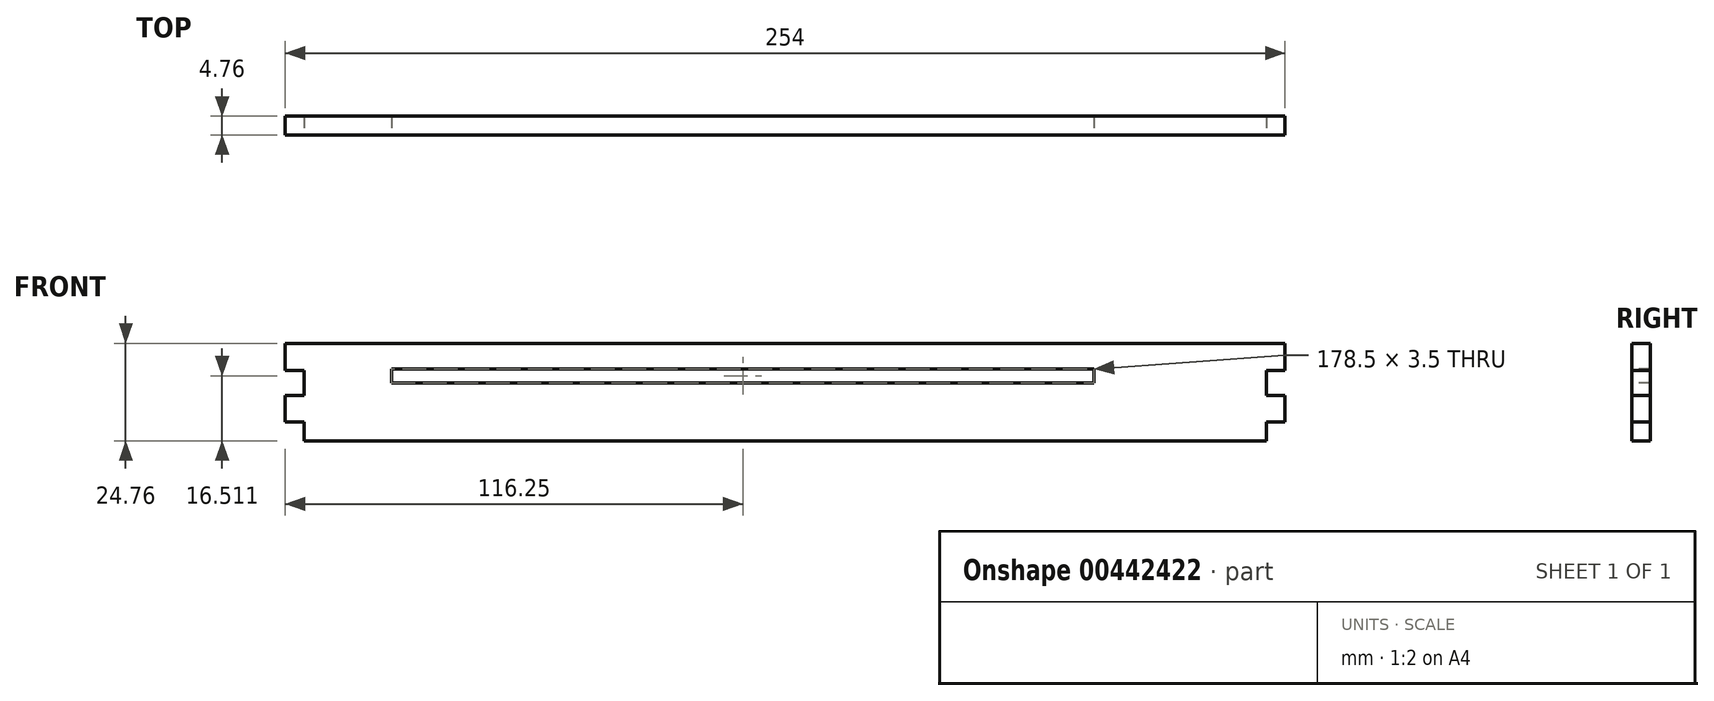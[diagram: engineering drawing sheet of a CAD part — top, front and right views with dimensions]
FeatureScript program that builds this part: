
annotation { "Feature Type Name" : "Feature", "Feature Type Description" : "" }
export const myFeature = defineFeature(function(context is Context, id is Id, definition is map)
    precondition{}
    {
        {
            var Q0;
            Q0=qCreatedBy(makeId("Front.planeOp"),FACE);
            var sketch = newSketch(context, id + "F0", { "sketchPlane" : qUnion([Q0])});
            skLineSegment(sketch, "E0.bottom", {"start": v(-127, 12.38) * mm, "end": v(127, 12.38) * mm});
            skLineSegment(sketch, "E0.top", {"start": v(-127, -12.38) * mm, "end": v(127, -12.38) * mm});
            skLineSegment(sketch, "E0.left", {"start": v(-127, 12.38) * mm, "end": v(-127, -12.38) * mm});
            skLineSegment(sketch, "E0.right", {"start": v(127, 12.38) * mm, "end": v(127, -12.38) * mm});
            skPoint(sketch, "E0.middle", {"position": v(0, 0) * mm});
            skSolve(sketch);
        }
        {
            var Q0;
            Q0 = qSketchRegion(id + "F0", true);
            extrude(context, id + "F1", {"entities" : qUnion([Q0]), "depth" : 4.76 * mm});
        }
        {
            var Q0;
            Q0=makeQuery(id+"F1.opExtrude","CAP_FACE",FACE,{"disambiguationData":[OSD([sQuery(id+"F0.wireOp",EDGE,"E0.bottom"),sQuery(id+"F0.wireOp",EDGE,"E0.top"),sQuery(id+"F0.wireOp",EDGE,"E0.left"),sQuery(id+"F0.wireOp",EDGE,"E0.right")])],"isStart":false});
            var sketch = newSketch(context, id + "F2", { "sketchPlane" : qUnion([Q0])});
            skLineSegment(sketch, "E1", {"start": v(-127, -7.62) * mm, "end": v(-127, 12.38) * mm, "construction": true});
            skLineSegment(sketch, "E2", {"start": v(-127, 2.38) * mm, "end": v(127, 2.38) * mm, "construction": true});
            skLineSegment(sketch, "E3.bottom", {"start": v(-122.24, 5.56) * mm, "end": v(-127, 5.56) * mm});
            skLineSegment(sketch, "E3.top", {"start": v(-122.24, -0.8) * mm, "end": v(-127, -0.8) * mm});
            skLineSegment(sketch, "E3.left", {"start": v(-122.24, 5.56) * mm, "end": v(-122.24, -0.8) * mm});
            skLineSegment(sketch, "E3.right", {"start": v(-127, 5.56) * mm, "end": v(-127, -0.8) * mm});
            skLineSegment(sketch, "E4", {"start": v(0, 0) * mm, "end": v(0, 12.38) * mm, "construction": true});
            skLineSegment(sketch, "E5.MirrorCS", {"start": v(122.24, 5.56) * mm, "end": v(127, 5.56) * mm});
            skLineSegment(sketch, "E6.MirrorCS", {"start": v(122.24, 5.56) * mm, "end": v(122.24, -0.8) * mm});
            skLineSegment(sketch, "E7.MirrorCS", {"start": v(122.24, -0.8) * mm, "end": v(127, -0.8) * mm});
            skLineSegment(sketch, "E8", {"start": v(127, 5.56) * mm, "end": v(127, -0.8) * mm});
            skLineSegment(sketch, "E9", {"start": v(127, -12.38) * mm, "end": v(-127, -12.38) * mm, "construction": true});
            skLineSegment(sketch, "E10", {"start": v(-127, -7.62) * mm, "end": v(127, -7.62) * mm, "construction": true});
            skSolve(sketch);
        }
        {
            var Q0;
            Q0 = qSketchRegion(id + "F2", true);
            extrude(context, id + "F3", {"entities" : qUnion([Q0]), "operationType" : NewBodyOperationType.REMOVE, "oppositeDirection" : true, "depth" : 25.4 * mm});
        }
        {
            var Q0;
            Q0=makeQuery(id+"F1.opExtrude","CAP_FACE",FACE,{"disambiguationData":[OSD([sQuery(id+"F0.wireOp",EDGE,"E0.bottom"),sQuery(id+"F0.wireOp",EDGE,"E0.top"),sQuery(id+"F0.wireOp",EDGE,"E0.left"),sQuery(id+"F0.wireOp",EDGE,"E0.right")])],"isStart":false});
            var sketch = newSketch(context, id + "F4", { "sketchPlane" : qUnion([Q0])});
            skLineSegment(sketch, "E11", {"start": v(127, -12.38) * mm, "end": v(122.24, -12.38) * mm});
            skLineSegment(sketch, "E12", {"start": v(122.24, -12.38) * mm, "end": v(122.24, -7.62) * mm});
            skLineSegment(sketch, "E13", {"start": v(122.24, -7.62) * mm, "end": v(127, -7.62) * mm});
            skLineSegment(sketch, "E14", {"start": v(127, -7.62) * mm, "end": v(127, -12.38) * mm});
            skLineSegment(sketch, "E15", {"start": v(0, 0) * mm, "end": v(0, 12.38) * mm, "construction": true});
            skLineSegment(sketch, "E16.MirrorCS", {"start": v(-122.24, -12.38) * mm, "end": v(-122.24, -7.62) * mm});
            skLineSegment(sketch, "E17.MirrorCS", {"start": v(-122.24, -7.62) * mm, "end": v(-127, -7.62) * mm});
            skLineSegment(sketch, "E18.MirrorCS", {"start": v(-127, -7.62) * mm, "end": v(-127, -12.38) * mm});
            skLineSegment(sketch, "E19.MirrorCS", {"start": v(-127, -12.38) * mm, "end": v(-122.24, -12.38) * mm});
            skSolve(sketch);
        }
        {
            var Q0;
            Q0 = qSketchRegion(id + "F4", true);
            extrude(context, id + "F5", {"entities" : qUnion([Q0]), "operationType" : NewBodyOperationType.REMOVE, "oppositeDirection" : true, "depth" : 25.4 * mm});
        }
        {
            var Q0;
            Q0=makeQuery(id+"F1.opExtrude","CAP_FACE",FACE,{"disambiguationData":[OSD([sQuery(id+"F0.wireOp",EDGE,"E0.bottom"),sQuery(id+"F0.wireOp",EDGE,"E0.top"),sQuery(id+"F0.wireOp",EDGE,"E0.left"),sQuery(id+"F0.wireOp",EDGE,"E0.right")])],"isStart":false});
            var sketch = newSketch(context, id + "F6", { "sketchPlane" : qUnion([Q0])});
            skLineSegment(sketch, "E20", {"start": v(-110, 12.38) * mm, "end": v(-110, -12.38) * mm, "construction": true});
            skLineSegment(sketch, "E21.bottom", {"start": v(-100, 2.38) * mm, "end": v(-92, 2.38) * mm});
            skLineSegment(sketch, "E21.top", {"start": v(-100, 5.88) * mm, "end": v(-92, 5.88) * mm});
            skLineSegment(sketch, "E21.left", {"start": v(-100, 2.38) * mm, "end": v(-100, 5.88) * mm});
            skLineSegment(sketch, "E21.right", {"start": v(-92, 2.38) * mm, "end": v(-92, 5.88) * mm});
            skLineSegment(sketch, "E22", {"start": v(-96, 5.88) * mm, "end": v(-96, 2.38) * mm, "construction": true});
            skLineSegment(sketch, "E23", {"start": v(-100, 2.38) * mm, "end": v(-122.24, 2.38) * mm, "construction": true});
            skLineSegment(sketch, "E24.1.0.0", {"start": v(-90.5, 5.88) * mm, "end": v(-90.5, 2.38) * mm, "construction": true});
            skLineSegment(sketch, "E24.1.0.1", {"start": v(-94.5, 5.88) * mm, "end": v(-86.5, 5.88) * mm});
            skLineSegment(sketch, "E24.1.0.2", {"start": v(-94.5, 2.38) * mm, "end": v(-94.5, 5.88) * mm});
            skLineSegment(sketch, "E24.1.0.3", {"start": v(-94.5, 2.38) * mm, "end": v(-86.5, 2.38) * mm});
            skLineSegment(sketch, "E24.1.0.4", {"start": v(-86.5, 2.38) * mm, "end": v(-86.5, 5.88) * mm});
            skLineSegment(sketch, "E24.2.0.0", {"start": v(-85, 5.88) * mm, "end": v(-85, 2.38) * mm, "construction": true});
            skLineSegment(sketch, "E24.2.0.1", {"start": v(-89, 5.88) * mm, "end": v(-81, 5.88) * mm});
            skLineSegment(sketch, "E24.2.0.2", {"start": v(-89, 2.38) * mm, "end": v(-89, 5.88) * mm});
            skLineSegment(sketch, "E24.2.0.3", {"start": v(-89, 2.38) * mm, "end": v(-81, 2.38) * mm});
            skLineSegment(sketch, "E24.2.0.4", {"start": v(-81, 2.38) * mm, "end": v(-81, 5.88) * mm});
            skLineSegment(sketch, "E24.3.0.0", {"start": v(-79.5, 5.88) * mm, "end": v(-79.5, 2.38) * mm, "construction": true});
            skLineSegment(sketch, "E24.3.0.1", {"start": v(-83.5, 5.88) * mm, "end": v(-75.5, 5.88) * mm});
            skLineSegment(sketch, "E24.3.0.2", {"start": v(-83.5, 2.38) * mm, "end": v(-83.5, 5.88) * mm});
            skLineSegment(sketch, "E24.3.0.3", {"start": v(-83.5, 2.38) * mm, "end": v(-75.5, 2.38) * mm});
            skLineSegment(sketch, "E24.3.0.4", {"start": v(-75.5, 2.38) * mm, "end": v(-75.5, 5.88) * mm});
            skLineSegment(sketch, "E24.4.0.0", {"start": v(-74, 5.88) * mm, "end": v(-74, 2.38) * mm, "construction": true});
            skLineSegment(sketch, "E24.4.0.1", {"start": v(-78, 5.88) * mm, "end": v(-70, 5.88) * mm});
            skLineSegment(sketch, "E24.4.0.2", {"start": v(-78, 2.38) * mm, "end": v(-78, 5.88) * mm});
            skLineSegment(sketch, "E24.4.0.3", {"start": v(-78, 2.38) * mm, "end": v(-70, 2.38) * mm});
            skLineSegment(sketch, "E24.4.0.4", {"start": v(-70, 2.38) * mm, "end": v(-70, 5.88) * mm});
            skLineSegment(sketch, "E24.5.0.0", {"start": v(-68.5, 5.88) * mm, "end": v(-68.5, 2.38) * mm, "construction": true});
            skLineSegment(sketch, "E24.5.0.1", {"start": v(-72.5, 5.88) * mm, "end": v(-64.5, 5.88) * mm});
            skLineSegment(sketch, "E24.5.0.2", {"start": v(-72.5, 2.38) * mm, "end": v(-72.5, 5.88) * mm});
            skLineSegment(sketch, "E24.5.0.3", {"start": v(-72.5, 2.38) * mm, "end": v(-64.5, 2.38) * mm});
            skLineSegment(sketch, "E24.5.0.4", {"start": v(-64.5, 2.38) * mm, "end": v(-64.5, 5.88) * mm});
            skLineSegment(sketch, "E24.6.0.0", {"start": v(-63, 5.88) * mm, "end": v(-63, 2.38) * mm, "construction": true});
            skLineSegment(sketch, "E24.6.0.1", {"start": v(-67, 5.88) * mm, "end": v(-59, 5.88) * mm});
            skLineSegment(sketch, "E24.6.0.2", {"start": v(-67, 2.38) * mm, "end": v(-67, 5.88) * mm});
            skLineSegment(sketch, "E24.6.0.3", {"start": v(-67, 2.38) * mm, "end": v(-59, 2.38) * mm});
            skLineSegment(sketch, "E24.6.0.4", {"start": v(-59, 2.38) * mm, "end": v(-59, 5.88) * mm});
            skLineSegment(sketch, "E24.7.0.0", {"start": v(-57.5, 5.88) * mm, "end": v(-57.5, 2.38) * mm, "construction": true});
            skLineSegment(sketch, "E24.7.0.1", {"start": v(-61.5, 5.88) * mm, "end": v(-53.5, 5.88) * mm});
            skLineSegment(sketch, "E24.7.0.2", {"start": v(-61.5, 2.38) * mm, "end": v(-61.5, 5.88) * mm});
            skLineSegment(sketch, "E24.7.0.3", {"start": v(-61.5, 2.38) * mm, "end": v(-53.5, 2.38) * mm});
            skLineSegment(sketch, "E24.7.0.4", {"start": v(-53.5, 2.38) * mm, "end": v(-53.5, 5.88) * mm});
            skLineSegment(sketch, "E24.8.0.0", {"start": v(-52, 5.88) * mm, "end": v(-52, 2.38) * mm, "construction": true});
            skLineSegment(sketch, "E24.8.0.1", {"start": v(-56, 5.88) * mm, "end": v(-48, 5.88) * mm});
            skLineSegment(sketch, "E24.8.0.2", {"start": v(-56, 2.38) * mm, "end": v(-56, 5.88) * mm});
            skLineSegment(sketch, "E24.8.0.3", {"start": v(-56, 2.38) * mm, "end": v(-48, 2.38) * mm});
            skLineSegment(sketch, "E24.8.0.4", {"start": v(-48, 2.38) * mm, "end": v(-48, 5.88) * mm});
            skLineSegment(sketch, "E24.9.0.0", {"start": v(-46.5, 5.88) * mm, "end": v(-46.5, 2.38) * mm, "construction": true});
            skLineSegment(sketch, "E24.9.0.1", {"start": v(-50.5, 5.88) * mm, "end": v(-42.5, 5.88) * mm});
            skLineSegment(sketch, "E24.9.0.2", {"start": v(-50.5, 2.38) * mm, "end": v(-50.5, 5.88) * mm});
            skLineSegment(sketch, "E24.9.0.3", {"start": v(-50.5, 2.38) * mm, "end": v(-42.5, 2.38) * mm});
            skLineSegment(sketch, "E24.9.0.4", {"start": v(-42.5, 2.38) * mm, "end": v(-42.5, 5.88) * mm});
            skLineSegment(sketch, "E24.10.0.0", {"start": v(-41, 5.88) * mm, "end": v(-41, 2.38) * mm, "construction": true});
            skLineSegment(sketch, "E24.10.0.1", {"start": v(-45, 5.88) * mm, "end": v(-37, 5.88) * mm});
            skLineSegment(sketch, "E24.10.0.2", {"start": v(-45, 2.38) * mm, "end": v(-45, 5.88) * mm});
            skLineSegment(sketch, "E24.10.0.3", {"start": v(-45, 2.38) * mm, "end": v(-37, 2.38) * mm});
            skLineSegment(sketch, "E24.10.0.4", {"start": v(-37, 2.38) * mm, "end": v(-37, 5.88) * mm});
            skLineSegment(sketch, "E24.11.0.0", {"start": v(-35.5, 5.88) * mm, "end": v(-35.5, 2.38) * mm, "construction": true});
            skLineSegment(sketch, "E24.11.0.1", {"start": v(-39.5, 5.88) * mm, "end": v(-31.5, 5.88) * mm});
            skLineSegment(sketch, "E24.11.0.2", {"start": v(-39.5, 2.38) * mm, "end": v(-39.5, 5.88) * mm});
            skLineSegment(sketch, "E24.11.0.3", {"start": v(-39.5, 2.38) * mm, "end": v(-31.5, 2.38) * mm});
            skLineSegment(sketch, "E24.11.0.4", {"start": v(-31.5, 2.38) * mm, "end": v(-31.5, 5.88) * mm});
            skLineSegment(sketch, "E24.12.0.0", {"start": v(-30, 5.88) * mm, "end": v(-30, 2.38) * mm, "construction": true});
            skLineSegment(sketch, "E24.12.0.1", {"start": v(-34, 5.88) * mm, "end": v(-26, 5.88) * mm});
            skLineSegment(sketch, "E24.12.0.2", {"start": v(-34, 2.38) * mm, "end": v(-34, 5.88) * mm});
            skLineSegment(sketch, "E24.12.0.3", {"start": v(-34, 2.38) * mm, "end": v(-26, 2.38) * mm});
            skLineSegment(sketch, "E24.12.0.4", {"start": v(-26, 2.38) * mm, "end": v(-26, 5.88) * mm});
            skLineSegment(sketch, "E24.13.0.0", {"start": v(-24.5, 5.88) * mm, "end": v(-24.5, 2.38) * mm, "construction": true});
            skLineSegment(sketch, "E24.13.0.1", {"start": v(-28.5, 5.88) * mm, "end": v(-20.5, 5.88) * mm});
            skLineSegment(sketch, "E24.13.0.2", {"start": v(-28.5, 2.38) * mm, "end": v(-28.5, 5.88) * mm});
            skLineSegment(sketch, "E24.13.0.3", {"start": v(-28.5, 2.38) * mm, "end": v(-20.5, 2.38) * mm});
            skLineSegment(sketch, "E24.13.0.4", {"start": v(-20.5, 2.38) * mm, "end": v(-20.5, 5.88) * mm});
            skLineSegment(sketch, "E24.14.0.0", {"start": v(-19, 5.88) * mm, "end": v(-19, 2.38) * mm, "construction": true});
            skLineSegment(sketch, "E24.14.0.1", {"start": v(-23, 5.88) * mm, "end": v(-15, 5.88) * mm});
            skLineSegment(sketch, "E24.14.0.2", {"start": v(-23, 2.38) * mm, "end": v(-23, 5.88) * mm});
            skLineSegment(sketch, "E24.14.0.3", {"start": v(-23, 2.38) * mm, "end": v(-15, 2.38) * mm});
            skLineSegment(sketch, "E24.14.0.4", {"start": v(-15, 2.38) * mm, "end": v(-15, 5.88) * mm});
            skLineSegment(sketch, "E24.15.0.0", {"start": v(-13.5, 5.88) * mm, "end": v(-13.5, 2.38) * mm, "construction": true});
            skLineSegment(sketch, "E24.15.0.1", {"start": v(-17.5, 5.88) * mm, "end": v(-9.5, 5.88) * mm});
            skLineSegment(sketch, "E24.15.0.2", {"start": v(-17.5, 2.38) * mm, "end": v(-17.5, 5.88) * mm});
            skLineSegment(sketch, "E24.15.0.3", {"start": v(-17.5, 2.38) * mm, "end": v(-9.5, 2.38) * mm});
            skLineSegment(sketch, "E24.15.0.4", {"start": v(-9.5, 2.38) * mm, "end": v(-9.5, 5.88) * mm});
            skLineSegment(sketch, "E24.16.0.0", {"start": v(-8, 5.88) * mm, "end": v(-8, 2.38) * mm, "construction": true});
            skLineSegment(sketch, "E24.16.0.1", {"start": v(-12, 5.88) * mm, "end": v(-4, 5.88) * mm});
            skLineSegment(sketch, "E24.16.0.2", {"start": v(-12, 2.38) * mm, "end": v(-12, 5.88) * mm});
            skLineSegment(sketch, "E24.16.0.3", {"start": v(-12, 2.38) * mm, "end": v(-4, 2.38) * mm});
            skLineSegment(sketch, "E24.16.0.4", {"start": v(-4, 2.38) * mm, "end": v(-4, 5.88) * mm});
            skLineSegment(sketch, "E24.17.0.0", {"start": v(-2.5, 5.88) * mm, "end": v(-2.5, 2.38) * mm, "construction": true});
            skLineSegment(sketch, "E24.17.0.1", {"start": v(-6.5, 5.88) * mm, "end": v(1.5, 5.88) * mm});
            skLineSegment(sketch, "E24.17.0.2", {"start": v(-6.5, 2.38) * mm, "end": v(-6.5, 5.88) * mm});
            skLineSegment(sketch, "E24.17.0.3", {"start": v(-6.5, 2.38) * mm, "end": v(1.5, 2.38) * mm});
            skLineSegment(sketch, "E24.17.0.4", {"start": v(1.5, 2.38) * mm, "end": v(1.5, 5.88) * mm});
            skLineSegment(sketch, "E24.18.0.0", {"start": v(3, 5.88) * mm, "end": v(3, 2.38) * mm, "construction": true});
            skLineSegment(sketch, "E24.18.0.1", {"start": v(-1, 5.88) * mm, "end": v(7, 5.88) * mm});
            skLineSegment(sketch, "E24.18.0.2", {"start": v(-1, 2.38) * mm, "end": v(-1, 5.88) * mm});
            skLineSegment(sketch, "E24.18.0.3", {"start": v(-1, 2.38) * mm, "end": v(7, 2.38) * mm});
            skLineSegment(sketch, "E24.18.0.4", {"start": v(7, 2.38) * mm, "end": v(7, 5.88) * mm});
            skLineSegment(sketch, "E24.19.0.0", {"start": v(8.5, 5.88) * mm, "end": v(8.5, 2.38) * mm, "construction": true});
            skLineSegment(sketch, "E24.19.0.1", {"start": v(4.5, 5.88) * mm, "end": v(12.5, 5.88) * mm});
            skLineSegment(sketch, "E24.19.0.2", {"start": v(4.5, 2.38) * mm, "end": v(4.5, 5.88) * mm});
            skLineSegment(sketch, "E24.19.0.3", {"start": v(4.5, 2.38) * mm, "end": v(12.5, 2.38) * mm});
            skLineSegment(sketch, "E24.19.0.4", {"start": v(12.5, 2.38) * mm, "end": v(12.5, 5.88) * mm});
            skLineSegment(sketch, "E24.20.0.0", {"start": v(14, 5.88) * mm, "end": v(14, 2.38) * mm, "construction": true});
            skLineSegment(sketch, "E24.20.0.1", {"start": v(10, 5.88) * mm, "end": v(18, 5.88) * mm});
            skLineSegment(sketch, "E24.20.0.2", {"start": v(10, 2.38) * mm, "end": v(10, 5.88) * mm});
            skLineSegment(sketch, "E24.20.0.3", {"start": v(10, 2.38) * mm, "end": v(18, 2.38) * mm});
            skLineSegment(sketch, "E24.20.0.4", {"start": v(18, 2.38) * mm, "end": v(18, 5.88) * mm});
            skLineSegment(sketch, "E24.21.0.0", {"start": v(19.5, 5.88) * mm, "end": v(19.5, 2.38) * mm, "construction": true});
            skLineSegment(sketch, "E24.21.0.1", {"start": v(15.5, 5.88) * mm, "end": v(23.5, 5.88) * mm});
            skLineSegment(sketch, "E24.21.0.2", {"start": v(15.5, 2.38) * mm, "end": v(15.5, 5.88) * mm});
            skLineSegment(sketch, "E24.21.0.3", {"start": v(15.5, 2.38) * mm, "end": v(23.5, 2.38) * mm});
            skLineSegment(sketch, "E24.21.0.4", {"start": v(23.5, 2.38) * mm, "end": v(23.5, 5.88) * mm});
            skLineSegment(sketch, "E24.22.0.0", {"start": v(25, 5.88) * mm, "end": v(25, 2.38) * mm, "construction": true});
            skLineSegment(sketch, "E24.22.0.1", {"start": v(21, 5.88) * mm, "end": v(29, 5.88) * mm});
            skLineSegment(sketch, "E24.22.0.2", {"start": v(21, 2.38) * mm, "end": v(21, 5.88) * mm});
            skLineSegment(sketch, "E24.22.0.3", {"start": v(21, 2.38) * mm, "end": v(29, 2.38) * mm});
            skLineSegment(sketch, "E24.22.0.4", {"start": v(29, 2.38) * mm, "end": v(29, 5.88) * mm});
            skLineSegment(sketch, "E24.23.0.0", {"start": v(30.5, 5.88) * mm, "end": v(30.5, 2.38) * mm, "construction": true});
            skLineSegment(sketch, "E24.23.0.1", {"start": v(26.5, 5.88) * mm, "end": v(34.5, 5.88) * mm});
            skLineSegment(sketch, "E24.23.0.2", {"start": v(26.5, 2.38) * mm, "end": v(26.5, 5.88) * mm});
            skLineSegment(sketch, "E24.23.0.3", {"start": v(26.5, 2.38) * mm, "end": v(34.5, 2.38) * mm});
            skLineSegment(sketch, "E24.23.0.4", {"start": v(34.5, 2.38) * mm, "end": v(34.5, 5.88) * mm});
            skLineSegment(sketch, "E24.24.0.0", {"start": v(36, 5.88) * mm, "end": v(36, 2.38) * mm, "construction": true});
            skLineSegment(sketch, "E24.24.0.1", {"start": v(32, 5.88) * mm, "end": v(40, 5.88) * mm});
            skLineSegment(sketch, "E24.24.0.2", {"start": v(32, 2.38) * mm, "end": v(32, 5.88) * mm});
            skLineSegment(sketch, "E24.24.0.3", {"start": v(32, 2.38) * mm, "end": v(40, 2.38) * mm});
            skLineSegment(sketch, "E24.24.0.4", {"start": v(40, 2.38) * mm, "end": v(40, 5.88) * mm});
            skLineSegment(sketch, "E24.25.0.0", {"start": v(41.5, 5.88) * mm, "end": v(41.5, 2.38) * mm, "construction": true});
            skLineSegment(sketch, "E24.25.0.1", {"start": v(37.5, 5.88) * mm, "end": v(45.5, 5.88) * mm});
            skLineSegment(sketch, "E24.25.0.2", {"start": v(37.5, 2.38) * mm, "end": v(37.5, 5.88) * mm});
            skLineSegment(sketch, "E24.25.0.3", {"start": v(37.5, 2.38) * mm, "end": v(45.5, 2.38) * mm});
            skLineSegment(sketch, "E24.25.0.4", {"start": v(45.5, 2.38) * mm, "end": v(45.5, 5.88) * mm});
            skLineSegment(sketch, "E24.26.0.0", {"start": v(47, 5.88) * mm, "end": v(47, 2.38) * mm, "construction": true});
            skLineSegment(sketch, "E24.26.0.1", {"start": v(43, 5.88) * mm, "end": v(51, 5.88) * mm});
            skLineSegment(sketch, "E24.26.0.2", {"start": v(43, 2.38) * mm, "end": v(43, 5.88) * mm});
            skLineSegment(sketch, "E24.26.0.3", {"start": v(43, 2.38) * mm, "end": v(51, 2.38) * mm});
            skLineSegment(sketch, "E24.26.0.4", {"start": v(51, 2.38) * mm, "end": v(51, 5.88) * mm});
            skLineSegment(sketch, "E24.27.0.0", {"start": v(52.5, 5.88) * mm, "end": v(52.5, 2.38) * mm, "construction": true});
            skLineSegment(sketch, "E24.27.0.1", {"start": v(48.5, 5.88) * mm, "end": v(56.5, 5.88) * mm});
            skLineSegment(sketch, "E24.27.0.2", {"start": v(48.5, 2.38) * mm, "end": v(48.5, 5.88) * mm});
            skLineSegment(sketch, "E24.27.0.3", {"start": v(48.5, 2.38) * mm, "end": v(56.5, 2.38) * mm});
            skLineSegment(sketch, "E24.27.0.4", {"start": v(56.5, 2.38) * mm, "end": v(56.5, 5.88) * mm});
            skLineSegment(sketch, "E24.28.0.0", {"start": v(58, 5.88) * mm, "end": v(58, 2.38) * mm, "construction": true});
            skLineSegment(sketch, "E24.28.0.1", {"start": v(54, 5.88) * mm, "end": v(62, 5.88) * mm});
            skLineSegment(sketch, "E24.28.0.2", {"start": v(54, 2.38) * mm, "end": v(54, 5.88) * mm});
            skLineSegment(sketch, "E24.28.0.3", {"start": v(54, 2.38) * mm, "end": v(62, 2.38) * mm});
            skLineSegment(sketch, "E24.28.0.4", {"start": v(62, 2.38) * mm, "end": v(62, 5.88) * mm});
            skLineSegment(sketch, "E24.29.0.0", {"start": v(63.5, 5.88) * mm, "end": v(63.5, 2.38) * mm, "construction": true});
            skLineSegment(sketch, "E24.29.0.1", {"start": v(59.5, 5.88) * mm, "end": v(67.5, 5.88) * mm});
            skLineSegment(sketch, "E24.29.0.2", {"start": v(59.5, 2.38) * mm, "end": v(59.5, 5.88) * mm});
            skLineSegment(sketch, "E24.29.0.3", {"start": v(59.5, 2.38) * mm, "end": v(67.5, 2.38) * mm});
            skLineSegment(sketch, "E24.29.0.4", {"start": v(67.5, 2.38) * mm, "end": v(67.5, 5.88) * mm});
            skLineSegment(sketch, "E24.30.0.0", {"start": v(69, 5.88) * mm, "end": v(69, 2.38) * mm, "construction": true});
            skLineSegment(sketch, "E24.30.0.1", {"start": v(65, 5.88) * mm, "end": v(73, 5.88) * mm});
            skLineSegment(sketch, "E24.30.0.2", {"start": v(65, 2.38) * mm, "end": v(65, 5.88) * mm});
            skLineSegment(sketch, "E24.30.0.3", {"start": v(65, 2.38) * mm, "end": v(73, 2.38) * mm});
            skLineSegment(sketch, "E24.30.0.4", {"start": v(73, 2.38) * mm, "end": v(73, 5.88) * mm});
            skLineSegment(sketch, "E24.31.0.0", {"start": v(74.5, 5.88) * mm, "end": v(74.5, 2.38) * mm, "construction": true});
            skLineSegment(sketch, "E24.31.0.1", {"start": v(70.5, 5.88) * mm, "end": v(78.5, 5.88) * mm});
            skLineSegment(sketch, "E24.31.0.2", {"start": v(70.5, 2.38) * mm, "end": v(70.5, 5.88) * mm});
            skLineSegment(sketch, "E24.31.0.3", {"start": v(70.5, 2.38) * mm, "end": v(78.5, 2.38) * mm});
            skLineSegment(sketch, "E24.31.0.4", {"start": v(78.5, 2.38) * mm, "end": v(78.5, 5.88) * mm});
            skLineSegment(sketch, "E24.direction1", {"start": v(-96, 2.38) * mm, "end": v(-90.5, 2.38) * mm, "construction": true});
            skSolve(sketch);
        }
        {
            var Q0;
            Q0 = qSketchRegion(id + "F6", true);
            extrude(context, id + "F7", {"entities" : qUnion([Q0]), "operationType" : NewBodyOperationType.REMOVE, "oppositeDirection" : true, "depth" : 25.4 * mm});
        }
    });
